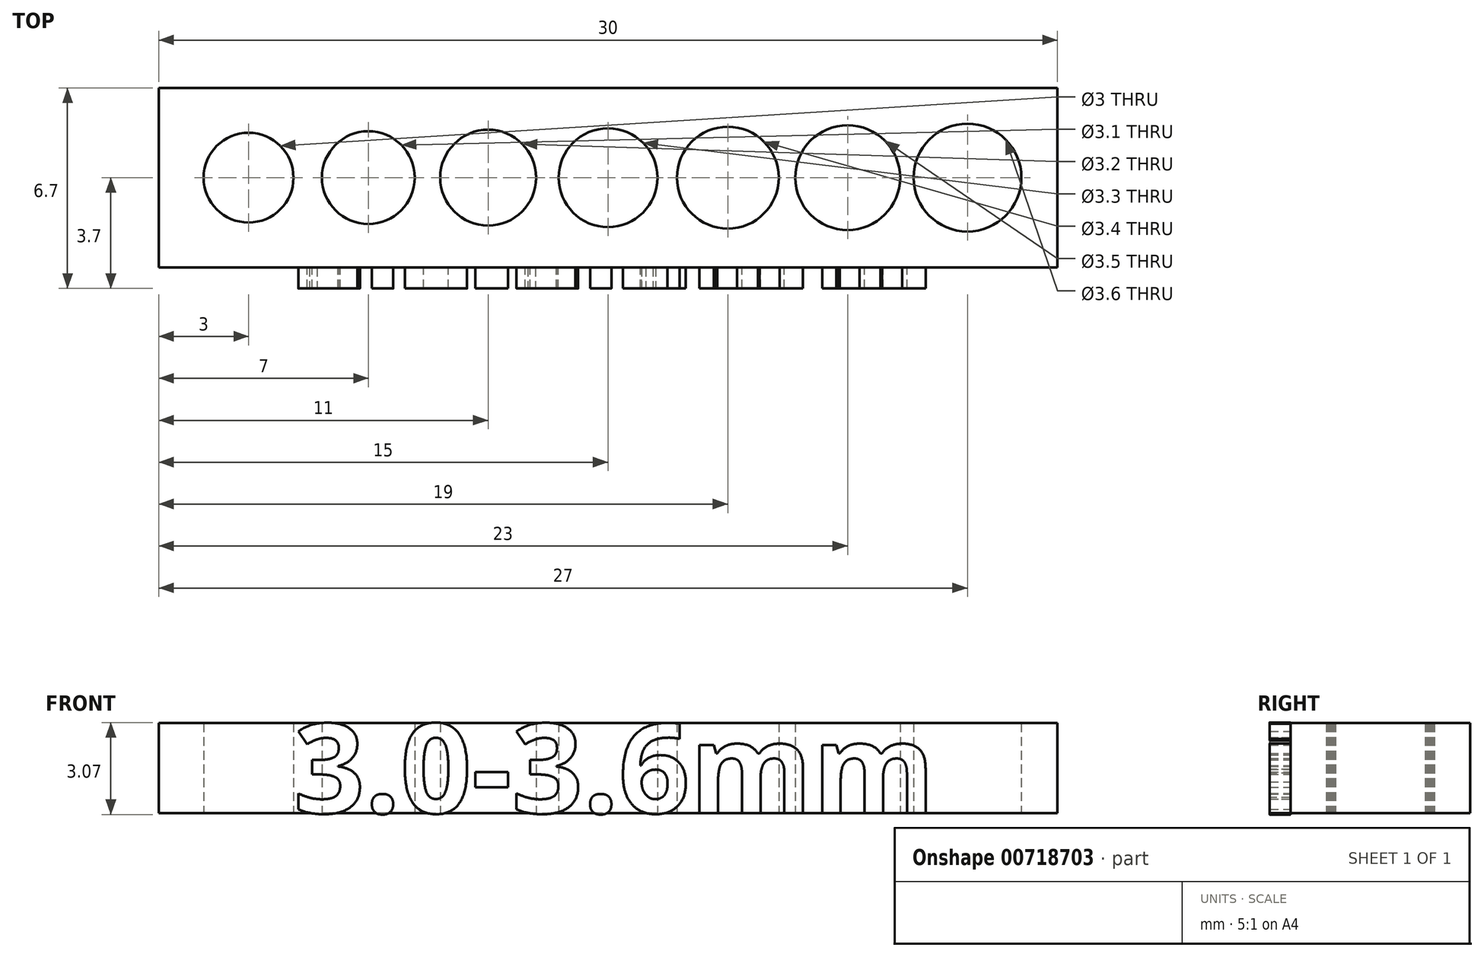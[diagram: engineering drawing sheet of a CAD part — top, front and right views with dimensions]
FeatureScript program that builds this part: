
annotation { "Feature Type Name" : "Feature", "Feature Type Description" : "" }
export const myFeature = defineFeature(function(context is Context, id is Id, definition is map)
    precondition{}
    {
        {
            var Q0;
            Q0=qCreatedBy(makeId("Top.planeOp"),FACE);
            var sketch = newSketch(context, id + "F0", { "sketchPlane" : qUnion([Q0])});
            skLineSegment(sketch, "E0.rect.bottom", {"start": v(-15, 3) * mm, "end": v(15, 3) * mm});
            skLineSegment(sketch, "E0.rect.top", {"start": v(-15, -3) * mm, "end": v(15, -3) * mm});
            skLineSegment(sketch, "E0.rect.left", {"start": v(-15, 3) * mm, "end": v(-15, -3) * mm});
            skLineSegment(sketch, "E0.rect.right", {"start": v(15, 3) * mm, "end": v(15, -3) * mm});
            skPoint(sketch, "E0.rect.middle", {"position": v(0, 0) * mm});
            skCircle(sketch, "E1", {"center": v(-12, 0) * mm, "radius": 1.5 * mm});
            skCircle(sketch, "E2", {"center": v(-8, 0) * mm, "radius": 1.55 * mm});
            skCircle(sketch, "E3", {"center": v(-4, 0) * mm, "radius": 1.6 * mm});
            skCircle(sketch, "E4", {"center": v(0, 0) * mm, "radius": 1.65 * mm});
            skCircle(sketch, "E5", {"center": v(4, 0) * mm, "radius": 1.7 * mm});
            skCircle(sketch, "E6", {"center": v(8, 0) * mm, "radius": 1.75 * mm});
            skCircle(sketch, "E7", {"center": v(12, 0) * mm, "radius": 1.8 * mm});
            skSolve(sketch);
        }
        {
            var Q0;
            Q0=qSketchRegion(id+"F0",true);
            extrude(context, id + "F1", {"entities" : qUnion([Q0]), "depth" : 3 * mm});
        }
        {
            var Q0;
            Q0=makeQuery(id+"F1.opExtrude","SWEPT_FACE",FACE,{"disambiguationData":[OSD([sQuery(id+"F0.wireOp",EDGE,"E0.rect.top")])]});
            var sketch = newSketch(context, id + "F2", { "sketchPlane" : qUnion([Q0])});
            skText(sketch, "E8", { "text": "3.0-3.6mm", "fontName": "OpenSans-Bold.ttf"});
            const initialGuessF2  = {"E8": [-0.0105, 0, 1, 0, 0.003]};
            skSetInitialGuess(sketch, initialGuessF2);
            skSolve(sketch);
        }
        {
            var Q0;
            Q0=qSketchRegion(id+"F2",true);
            extrude(context, id + "F3", {"entities" : qUnion([Q0]), "operationType" : NewBodyOperationType.ADD, "depth" : .7 * mm});
        }
    });
